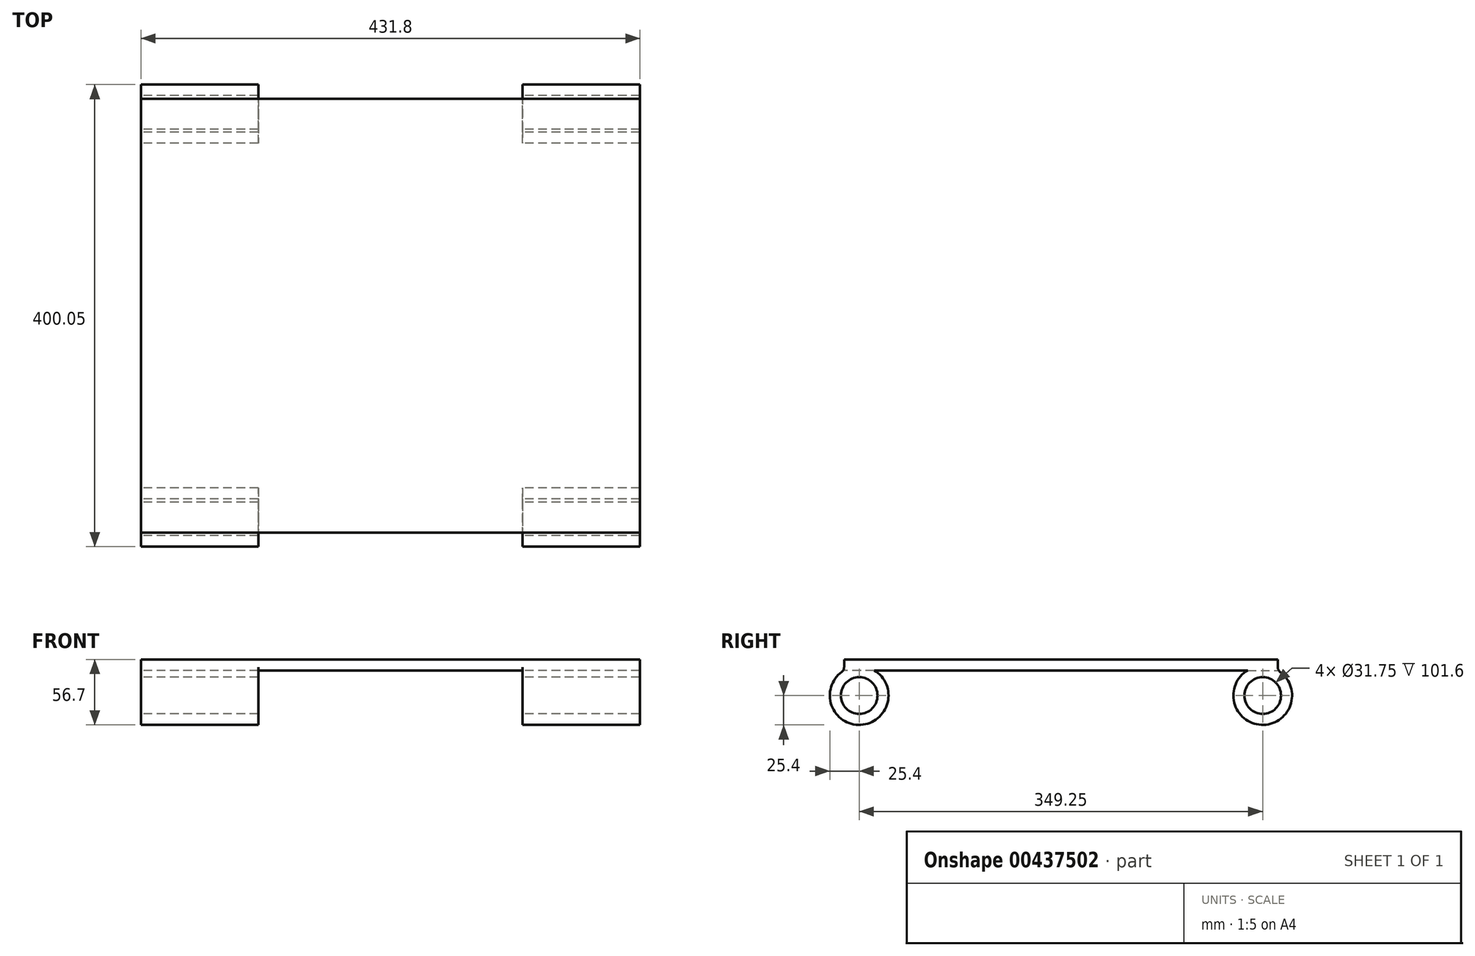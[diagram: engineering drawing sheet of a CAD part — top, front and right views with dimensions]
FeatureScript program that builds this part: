
annotation { "Feature Type Name" : "Feature", "Feature Type Description" : "" }
export const myFeature = defineFeature(function(context is Context, id is Id, definition is map)
    precondition{}
    {
        {
            var Q0;
            Q0=qCreatedBy(makeId("Right.planeOp"),FACE);
            var sketch = newSketch(context, id + "F0", { "sketchPlane" : qUnion([Q0])});
            skArc(sketch, "E0", {"start": v(-13.08, 21.77) * mm, "mid": v(0, -25.4) * mm, "end": v(13.08, 21.77) * mm});
            skLineSegment(sketch, "E1", {"start": v(-342.52, 24.95) * mm, "end": v(-342.52, 31.3) * mm});
            skLineSegment(sketch, "E2", {"start": v(-342.52, 31.3) * mm, "end": v(13.08, 31.3) * mm});
            skCircle(sketch, "E3", {"center": v(0, 0) * mm, "radius": 15.88 * mm});
            skLineSegment(sketch, "E4", {"start": v(-13.08, 21.77) * mm, "end": v(-342.52, 21.77) * mm});
            skLineSegment(sketch, "E5", {"start": v(-342.52, 21.77) * mm, "end": v(-342.52, 24.95) * mm});
            skLineSegment(sketch, "E6", {"start": v(13.08, 21.77) * mm, "end": v(13.08, 31.3) * mm});
            skPoint(sketch, "E7.start.orphan", {"position": v(154.04, 31.3) * mm});
            skPoint(sketch, "E8.end.orphan", {"position": v(154.04, 24.95) * mm});
            skPoint(sketch, "E8.start.orphan", {"position": v(154.04, 21.77) * mm});
            skSolve(sketch);
        }
        {
            var Q0;
            Q0 = qSketchRegion(id + "F0", true);
            extrude(context, id + "F1", {"entities" : qUnion([Q0]), "depth" : 431.8 * mm, "offsetDistance" : 25.4 * mm});
        }
        {
            var Q0;
            Q0=makeQuery(id+"F1.opExtrude","SWEPT_FACE",FACE,{"disambiguationData":[OSD([sQuery(id+"F0.wireOp",EDGE,"E6")])]});
            var sketch = newSketch(context, id + "F2", { "sketchPlane" : qUnion([Q0])});
            skLineSegment(sketch, "E9", {"start": v(-215.9, 21.77) * mm, "end": v(-330.2, 21.77) * mm});
            skLineSegment(sketch, "E10", {"start": v(-330.2, 21.77) * mm, "end": v(-330.2, -30.45) * mm});
            skLineSegment(sketch, "E11", {"start": v(-330.2, -30.45) * mm, "end": v(-228.6, -30.45) * mm});
            skLineSegment(sketch, "E12", {"start": v(-228.6, -30.45) * mm, "end": v(-101.6, -30.45) * mm});
            skLineSegment(sketch, "E13", {"start": v(-101.6, -30.45) * mm, "end": v(-101.6, 21.77) * mm});
            skLineSegment(sketch, "E14", {"start": v(-101.6, 21.77) * mm, "end": v(-215.9, 21.77) * mm});
            skSolve(sketch);
        }
        {
            var Q0;
            Q0 = qSketchRegion(id + "F2", true);
            extrude(context, id + "F3", {"entities" : qUnion([Q0]), "operationType" : NewBodyOperationType.REMOVE, "oppositeDirection" : true, "depth" : 67.06 * mm, "offsetDistance" : 25.4 * mm, "hasSecondDirection" : true, "secondDirectionOppositeDirection" : false, "secondDirectionDepth" : 51.82 * mm});
        }
        {
            var Q0;
            Q0=qCreatedBy(makeId("Front.planeOp"),FACE);
            cPlane(context, id + "F4", {"entities" : qUnion([Q0]), "cplaneType" : CPlaneType.OFFSET, "offset" : 174.62 * mm, "width" : 152.4 * mm, "height" : 152.4 * mm});
        }
        {
            var Q0;
            Q0=makeQuery(id+"F1.opExtrude","SWEPT_BODY",BODY,{"disambiguationData":[OSD([sQuery(id+"F0.wireOp",EDGE,"E0"),sQuery(id+"F0.wireOp",EDGE,"E1"),sQuery(id+"F0.wireOp",EDGE,"E2"),sQuery(id+"F0.wireOp",EDGE,"E3"),sQuery(id+"F0.wireOp",EDGE,"E4"),sQuery(id+"F0.wireOp",EDGE,"E5"),sQuery(id+"F0.wireOp",EDGE,"E6")])]});
            var Q1;
            Q1=qCreatedBy(id+"F4.planeOp",FACE);
            mirror(context, id + "F5", {"operationType" : NewBodyOperationType.ADD, "entities" : qUnion([Q0]), "mirrorPlane" : qUnion([Q1])});
        }
        {
            var Q0;
            {var subQ0=sQuery(id+"F0.wireOp",EDGE,"E6");var subQ1=makeQuery(id+"F1.opExtrude","SWEPT_FACE",FACE,{"disambiguationData":[OSD([subQ0])]});var subQ3=sQuery(id+"F0.wireOp",EDGE,"E0");var subQ4=makeQuery(id+"F1.opExtrude","SWEPT_FACE",FACE,{"disambiguationData":[OSD([subQ3])]});Q0=makeQuery(id+"F3.boolean.opBoolean","SPLIT",EDGE,{"disambiguationData":[topologyDisambiguationEdgeConnected([subQ4,subQ1]),TD([makeQuery(id+"F3.opExtrude","SWEPT_FACE",FACE,{"disambiguationData":[OSD([sQuery(id+"F2.wireOp",EDGE,"E13")])]})])],"derivedFrom":makeQuery(id+"F1.opExtrude","SWEPT_EDGE",EDGE,{"disambiguationData":[OSD([subQ3,subQ0])]})});}
            var Q1;
            {var subQ1=sQuery(id+"F0.wireOp",EDGE,"E6");var subQ2=makeQuery(id+"F1.opExtrude","SWEPT_FACE",FACE,{"disambiguationData":[OSD([subQ1])]});var subQ3=sQuery(id+"F0.wireOp",EDGE,"E0");var subQ4=makeQuery(id+"F1.opExtrude","SWEPT_FACE",FACE,{"disambiguationData":[OSD([subQ3])]});Q1=makeQuery(id+"F3.boolean.opBoolean","SPLIT",EDGE,{"disambiguationData":[topologyDisambiguationEdgeConnected([subQ4,subQ2]),TD([makeQuery(id+"F3.opExtrude","SWEPT_FACE",FACE,{"disambiguationData":[OSD([sQuery(id+"F2.wireOp",EDGE,"E10")])]})])],"derivedFrom":makeQuery(id+"F1.opExtrude","SWEPT_EDGE",EDGE,{"disambiguationData":[OSD([subQ3,subQ1])]})});}
            fillet(context, id + "F6", {"entities" : qUnion([Q0, Q1]), "radius" : 5.08 * mm, "tangentPropagation" : true, "allowEdgeOverflow" : false});
        }
        {
            var Q0;
            {var subQ0=sQuery(id+"F0.wireOp",EDGE,"E6");var subQ1=makeQuery(id+"F1.opExtrude","SWEPT_FACE",FACE,{"disambiguationData":[OSD([subQ0])]});var subQ3=sQuery(id+"F0.wireOp",EDGE,"E0");var subQ4=makeQuery(id+"F1.opExtrude","SWEPT_FACE",FACE,{"disambiguationData":[OSD([subQ3])]});Q0=makeQuery(id+"F5.opPattern","COPY",EDGE,{"derivedFrom":makeQuery(id+"F3.boolean.opBoolean","SPLIT",EDGE,{"disambiguationData":[topologyDisambiguationEdgeConnected([subQ4,subQ1]),TD([makeQuery(id+"F3.opExtrude","SWEPT_FACE",FACE,{"disambiguationData":[OSD([sQuery(id+"F2.wireOp",EDGE,"E13")])]})])],"derivedFrom":makeQuery(id+"F1.opExtrude","SWEPT_EDGE",EDGE,{"disambiguationData":[OSD([subQ3,subQ0])]})}),"instanceName":"1"});}
            var Q1;
            {var subQ1=sQuery(id+"F0.wireOp",EDGE,"E6");var subQ2=makeQuery(id+"F1.opExtrude","SWEPT_FACE",FACE,{"disambiguationData":[OSD([subQ1])]});var subQ3=sQuery(id+"F0.wireOp",EDGE,"E0");var subQ4=makeQuery(id+"F1.opExtrude","SWEPT_FACE",FACE,{"disambiguationData":[OSD([subQ3])]});Q1=makeQuery(id+"F5.opPattern","COPY",EDGE,{"derivedFrom":makeQuery(id+"F3.boolean.opBoolean","SPLIT",EDGE,{"disambiguationData":[topologyDisambiguationEdgeConnected([subQ4,subQ2]),TD([makeQuery(id+"F3.opExtrude","SWEPT_FACE",FACE,{"disambiguationData":[OSD([sQuery(id+"F2.wireOp",EDGE,"E10")])]})])],"derivedFrom":makeQuery(id+"F1.opExtrude","SWEPT_EDGE",EDGE,{"disambiguationData":[OSD([subQ3,subQ1])]})}),"instanceName":"1"});}
            fillet(context, id + "F7", {"entities" : qUnion([Q0, Q1]), "radius" : 5.08 * mm, "tangentPropagation" : true, "allowEdgeOverflow" : false});
        }
    });
